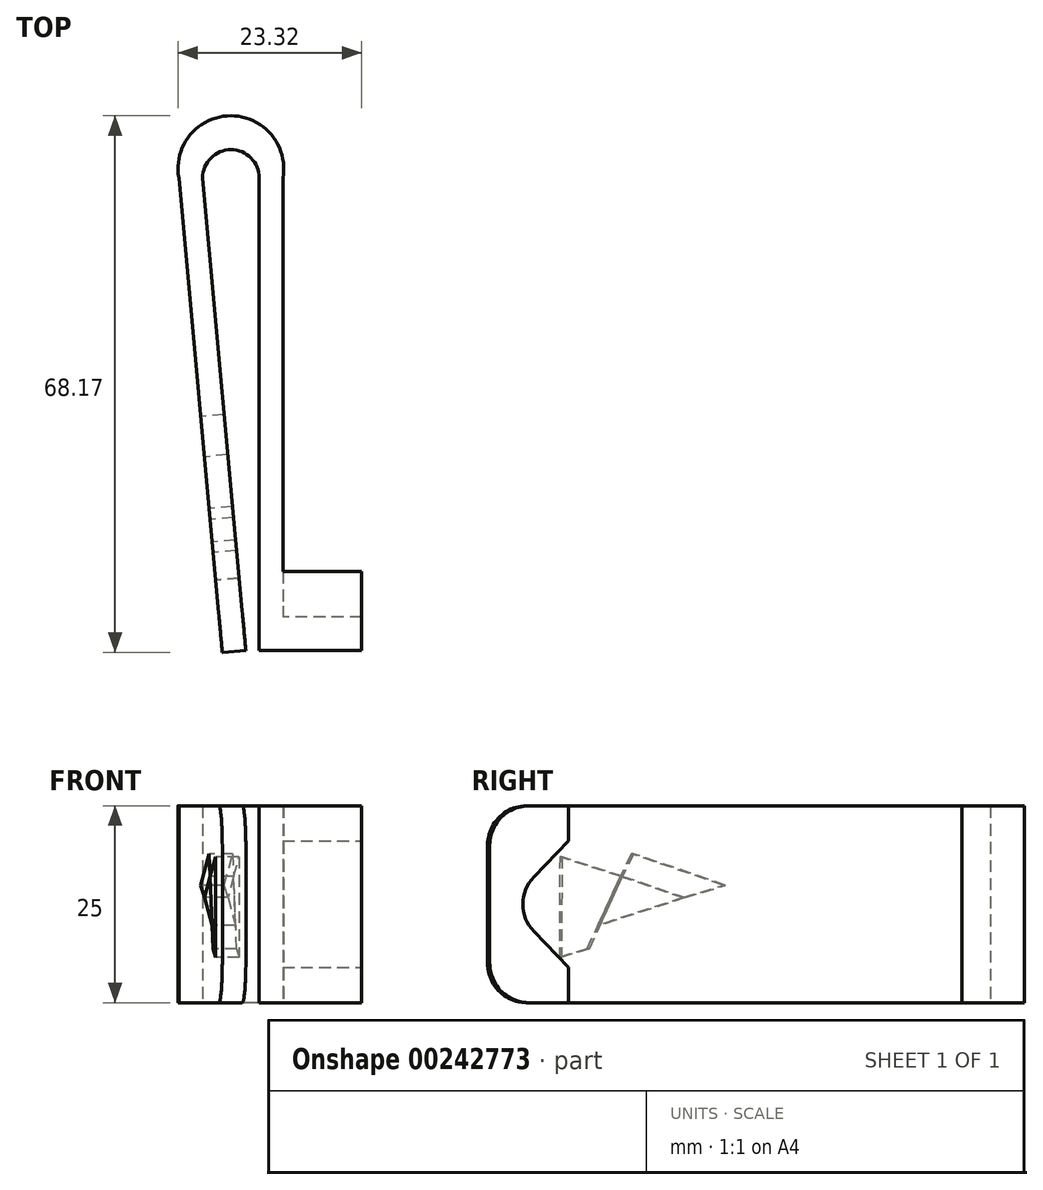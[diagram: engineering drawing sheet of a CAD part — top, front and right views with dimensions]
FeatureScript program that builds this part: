
annotation { "Feature Type Name" : "Feature", "Feature Type Description" : "" }
export const myFeature = defineFeature(function(context is Context, id is Id, definition is map)
    precondition{}
    {
        {
            var Q0;
            Q0=qCreatedBy(makeId("Top.planeOp"),FACE);
            var sketch = newSketch(context, id + "F0", { "sketchPlane" : qUnion([Q0])});
            skArc(sketch, "E0", {"start": v(3.6, 0) * mm, "mid": v(0, 3.6) * mm, "end": v(-3.6, 0) * mm});
            skLineSegment(sketch, "E1", {"start": v(3.6, 0) * mm, "end": v(3.6, -60) * mm});
            skLineSegment(sketch, "E2", {"start": v(-3.6, 0) * mm, "end": v(1.9, -60) * mm});
            skLineSegment(sketch, "E3", {"start": v(1.9, -60) * mm, "end": v(-1.1, -60.27) * mm});
            skLineSegment(sketch, "E4", {"start": v(3.6, -60) * mm, "end": v(6.6, -60) * mm});
            skLineSegment(sketch, "E5", {"start": v(6.6, -46.61) * mm, "end": v(6.6, 0) * mm});
            skLineSegment(sketch, "E6", {"start": v(-1.1, -60.27) * mm, "end": v(-6.61, 0) * mm});
            skArc(sketch, "E7", {"start": v(6.6, 0) * mm, "mid": v(0, 7.9) * mm, "end": v(-6.61, 0) * mm});
            skLineSegment(sketch, "E8", {"start": v(6.6, -60) * mm, "end": v(16.6, -60) * mm});
            skLineSegment(sketch, "E9", {"start": v(16.6, -60) * mm, "end": v(16.6, -50) * mm});
            skLineSegment(sketch, "E10", {"start": v(6.6, -46.61) * mm, "end": v(6.6, -50) * mm});
            skLineSegment(sketch, "E11", {"start": v(6.6, -50) * mm, "end": v(16.6, -50) * mm});
            skSolve(sketch);
        }
        {
            var Q0;
            Q0=makeQuery(id+"F0.imprint","IMPRINT",FACE,{"disambiguationData":[TD([[makeQuery(id+"F0.imprint","IMPRINT",EDGE,{"derivedFrom":sQuery(id+"F0.wireOp",EDGE,"E0")}),-1.0]])]});
            extrude(context, id + "F1", {"entities" : qUnion([Q0]), "depth" : 25 * mm});
        }
        {
            var Q0;
            Q0=makeQuery(id+"F1.opExtrude","SWEPT_FACE",FACE,{"disambiguationData":[OSD([sQuery(id+"F0.wireOp",EDGE,"E9")])]});
            cPlane(context, id + "F2", {"entities" : qUnion([Q0]), "cplaneType" : CPlaneType.OFFSET, "offset" : 0 * mm, "width" : 150 * mm, "height" : 150 * mm});
        }
        {
            var Q0;
            Q0=qCreatedBy(id+"F2.planeOp",FACE);
            var sketch = newSketch(context, id + "F3", { "sketchPlane" : qUnion([Q0])});
            skPoint(sketch, "E12.0", {"position": v(-60, 12.5) * mm});
            skLineSegment(sketch, "E13", {"start": v(-60, 12.5) * mm, "end": v(-73.53, 12.5) * mm, "construction": true});
            skPoint(sketch, "E14.0", {"position": v(-60, 25) * mm});
            skPoint(sketch, "E15.0", {"position": v(0, 25) * mm});
            skPoint(sketch, "E16.start.orphan", {"position": v(-67.28, 12.5) * mm});
            skPoint(sketch, "E17.end.orphan", {"position": v(0, 0) * mm});
            skLineSegment(sketch, "E18", {"start": v(-60, 12.5) * mm, "end": v(-49.83, 12.5) * mm, "construction": true});
            skLineSegment(sketch, "E19.0", {"start": v(-50, 25) * mm, "end": v(-50, 0) * mm, "construction": true});
            skLineSegment(sketch, "E20", {"start": v(-50, 20.54) * mm, "end": v(-57.71, 12.5) * mm, "construction": true});
            skLineSegment(sketch, "E21", {"start": v(-50, 20.54) * mm, "end": v(-57.71, 12.5) * mm});
            skLineSegment(sketch, "E22.MirrorCS", {"start": v(-50, 4.46) * mm, "end": v(-57.71, 12.5) * mm, "construction": true});
            skLineSegment(sketch, "E23.MirrorCS", {"start": v(-50, 0) * mm, "end": v(-50, 25) * mm, "construction": true});
            skLineSegment(sketch, "E24", {"start": v(-57.71, 12.5) * mm, "end": v(-50, 4.46) * mm});
            skLineSegment(sketch, "E25", {"start": v(-50, 20.54) * mm, "end": v(-50, 4.46) * mm});
            skPoint(sketch, "E26.end.orphan", {"position": v(-50, 23.26) * mm});
            skPoint(sketch, "E27.end.orphan", {"position": v(-53.26, 23.26) * mm});
            skPoint(sketch, "E27.start.orphan", {"position": v(-53.26, 17.14) * mm});
            skPoint(sketch, "E28.MirrorCS.end.orphan", {"position": v(-53.26, 1.74) * mm});
            skPoint(sketch, "E28.MirrorCS.start.orphan", {"position": v(-53.26, 7.86) * mm});
            skPoint(sketch, "E29.MirrorCS.end.orphan", {"position": v(-50, 1.74) * mm});
            skSolve(sketch);
        }
        {
            var Q0;
            Q0=makeQuery(id+"F3.imprint","IMPRINT",FACE,{"disambiguationData":[TD([[makeQuery(id+"F3.imprint","IMPRINT",EDGE,{"derivedFrom":sQuery(id+"F3.wireOp",EDGE,"E21")}),1.0]])]});
            extrude(context, id + "F4", {"entities" : qUnion([Q0]), "operationType" : NewBodyOperationType.REMOVE, "oppositeDirection" : true, "depth" : 10 * mm});
        }
        {
            var Q0;
            Q0=makeQuery(id+"F4.boolean.opBoolean","COPY",EDGE,{"derivedFrom":makeQuery(id+"F4.opExtrude","SWEPT_EDGE",EDGE,{"disambiguationData":[OSD([sQuery(id+"F3.wireOp",EDGE,"E21"),sQuery(id+"F3.wireOp",EDGE,"E24")])]})});
            fillet(context, id + "F5", {"entities" : qUnion([Q0]), "radius" : 5 * mm, "tangentPropagation" : true, "allowEdgeOverflow" : false});
        }
        {
            var Q0;
            Q0=makeQuery(id+"F1.opExtrude","CAP_EDGE",EDGE,{"disambiguationData":[OSD([sQuery(id+"F0.wireOp",EDGE,"E4"),sQuery(id+"F0.wireOp",EDGE,"E8")])],"isStart":false});
            var Q1;
            Q1=makeQuery(id+"F1.opExtrude","CAP_EDGE",EDGE,{"disambiguationData":[OSD([sQuery(id+"F0.wireOp",EDGE,"E3")])],"isStart":false});
            var Q2;
            Q2=makeQuery(id+"F1.opExtrude","CAP_EDGE",EDGE,{"disambiguationData":[OSD([sQuery(id+"F0.wireOp",EDGE,"E3")])],"isStart":true});
            var Q3;
            Q3=makeQuery(id+"F1.opExtrude","CAP_EDGE",EDGE,{"disambiguationData":[OSD([sQuery(id+"F0.wireOp",EDGE,"E4"),sQuery(id+"F0.wireOp",EDGE,"E8")])],"isStart":true});
            fillet(context, id + "F6", {"entities" : qUnion([Q0, Q1, Q2, Q3]), "radius" : 5 * mm, "tangentPropagation" : true, "allowEdgeOverflow" : false});
        }
        {
            var Q0;
            Q0=makeQuery(id+"F1.opExtrude","SWEPT_FACE",FACE,{"disambiguationData":[OSD([sQuery(id+"F0.wireOp",EDGE,"E6")])]});
            cPlane(context, id + "F7", {"entities" : qUnion([Q0]), "cplaneType" : CPlaneType.OFFSET, "offset" : 0 * mm, "width" : 150 * mm, "height" : 150 * mm});
        }
        {
            var Q0;
            Q0=qCreatedBy(id+"F7.planeOp",FACE);
            var sketch = newSketch(context, id + "F8", { "sketchPlane" : qUnion([Q0])});
            skLineSegment(sketch, "E30", {"start": v(50.7, 18.52) * mm, "end": v(50.76, 5.76) * mm});
            skLineSegment(sketch, "E31", {"start": v(47.2, 6.86) * mm, "end": v(42.96, 16.05) * mm});
            skLineSegment(sketch, "E32", {"start": v(42.96, 16.05) * mm, "end": v(50.7, 18.52) * mm});
            skLineSegment(sketch, "E33", {"start": v(47.2, 6.86) * mm, "end": v(50.76, 5.76) * mm});
            skSolve(sketch);
        }
        {
            var Q0;
            Q0=makeQuery(id+"F8.imprint","IMPRINT",FACE,{"disambiguationData":[TD([[makeQuery(id+"F8.imprint","IMPRINT",EDGE,{"derivedFrom":sQuery(id+"F8.wireOp",EDGE,"E30")}),-1.0]])]});
            var Q1;
            Q1=sQuery(id+"F8.wireOp",EDGE,"E33");
            var Q2;
            Q2=sQuery(id+"F8.wireOp",EDGE,"E31");
            var Q3;
            Q3=sQuery(id+"F8.wireOp",EDGE,"E32");
            var Q4;
            Q4=sQuery(id+"F8.wireOp",EDGE,"E30");
            extrude(context, id + "F9", {"entities" : qUnion([Q0]), "operationType" : NewBodyOperationType.REMOVE, "surfaceEntities" : qUnion([Q1, Q2, Q3, Q4]), "oppositeDirection" : true, "depth" : 3 * mm});
        }
        {
            var Q0;
            Q0=qCreatedBy(id+"F7.planeOp",FACE);
            var sketch = newSketch(context, id + "F10", { "sketchPlane" : qUnion([Q0])});
            skLineSegment(sketch, "E34.0", {"start": v(45.84, 9.82) * mm, "end": v(42.96, 16.05) * mm});
            skLineSegment(sketch, "E35", {"start": v(42.96, 16.05) * mm, "end": v(34.97, 13.35) * mm});
            skLineSegment(sketch, "E36", {"start": v(34.97, 13.35) * mm, "end": v(45.84, 9.82) * mm});
            skPoint(sketch, "E37.orphan", {"position": v(47.2, 6.86) * mm});
            skSolve(sketch);
        }
        {
            var Q0;
            Q0 = qSketchRegion(id + "F8", true);
            extrude(context, id + "F11", {"entities" : qUnion([Q0]), "oppositeDirection" : true, "depth" : 3 * mm});
        }
        {
            var Q0;
            Q0=makeQuery(id+"F10.imprint","IMPRINT",FACE,{"disambiguationData":[TD([[makeQuery(id+"F10.imprint","IMPRINT",EDGE,{"derivedFrom":sQuery(id+"F10.wireOp",EDGE,"E34.0")}),1.0]])]});
            var Q1;
            Q1 = qSketchRegion(id + "F10", true);
            extrude(context, id + "F12", {"entities" : qUnion([Q0, Q1]), "operationType" : NewBodyOperationType.REMOVE, "oppositeDirection" : true, "depth" : 3 * mm});
        }
        {
            var Q0;
            Q0 = qSketchRegion(id + "F10", true);
            extrude(context, id + "F13", {"entities" : qUnion([Q0]), "oppositeDirection" : true, "depth" : 3 * mm});
        }
        {
            var Q0;
            Q0=qCreatedBy(id+"F7.planeOp",FACE);
            var sketch = newSketch(context, id + "F14", { "sketchPlane" : qUnion([Q0])});
            skLineSegment(sketch, "E38.0", {"start": v(42.96, 16.05) * mm, "end": v(34.97, 13.35) * mm});
            skLineSegment(sketch, "E39", {"start": v(34.97, 13.35) * mm, "end": v(29.85, 14.93) * mm});
            skLineSegment(sketch, "E40", {"start": v(29.85, 14.93) * mm, "end": v(41.59, 18.92) * mm});
            skLineSegment(sketch, "E41", {"start": v(41.59, 18.92) * mm, "end": v(42.96, 16.05) * mm});
            skPoint(sketch, "E42.0.end.orphan", {"position": v(45.84, 9.82) * mm});
            skSolve(sketch);
        }
        {
            var Q0;
            Q0=makeQuery(id+"F14.imprint","IMPRINT",FACE,{"disambiguationData":[TD([[makeQuery(id+"F14.imprint","IMPRINT",EDGE,{"derivedFrom":sQuery(id+"F14.wireOp",EDGE,"E38.0")}),-1.0]])]});
            extrude(context, id + "F15", {"entities" : qUnion([Q0]), "operationType" : NewBodyOperationType.REMOVE, "oppositeDirection" : true, "depth" : 3 * mm});
        }
        {
            var Q0;
            Q0 = qSketchRegion(id + "F14", true);
            extrude(context, id + "F16", {"entities" : qUnion([Q0]), "oppositeDirection" : true, "depth" : 3 * mm});
        }
    });
